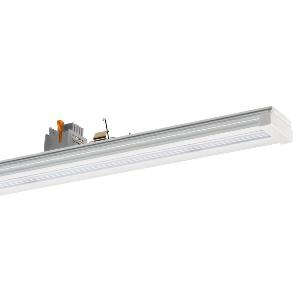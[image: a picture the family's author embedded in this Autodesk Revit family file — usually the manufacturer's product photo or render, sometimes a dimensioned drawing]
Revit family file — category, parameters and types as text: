
# Revit family: conveo_-_cvg_4500_850_xn-p_da_7_226848149-00804952_2d80
name_source: partatom
category: Lighting Fixtures
units: mm (PartAtom-declared; Revit-internal decimal feet)

## family parameters
Cut with Voids When Loaded = No
Host = Face
Light Source = No
Part Type = Normal
Room Calculation Point = No
Round Connector Dimension = Use Diameter
Shared = No

## types (1)
- CONVEO - CVG 4500/850/xN-P/DA/7 (1 x LED, 4300 lm, 5000K)
    Apparent Load = 28 VA
    Approval mark = CE
    CIE Flux Codes = 57 84 97 100 100
    Color Rendering = 80-89
    Color Temperature = 5000K
    Control Gear = Electronic ballast
    Default Elevation = 1800 mm
    Description = CVG 4500/850/xN-P/DA/7|Continuous-row system|light source: LED|work equipment: Adjustable electronic ballast, digital DALI|connected load: 220-240 V, 50-60 Hz|Power consumption: approx. 28 W|luminous flux: 4300 lm|luminous efficacy: 153 lm/W|colour temperature: Cold white, ca. 5000 K|color rendering index (CRI): >= 80|chromaticity tolerance:  3 SDCM|System of protection: IP 54|class of protection: I|technology: Continuously dimmable|luminaire body|material: Aluminium|surface: Powder coatet|colour: White|lamp cover: Acrylic (PMMA), Satine|weight (net): approx. 1.9 kg|Fastening: Available separately|minimum ambient temperature: -25 ░C|maximum ambient temperature: 55 ░C|glare control: Prism optics (linear)|Approval mark: VDE - ENEC|
    Frequency = 50 Hz
    Height = 70 mm
    Lamp = 1 x LED
    Lamp Light Flux = 4300 lm
    Lamp count = 1
    Length = 1500 mm
    Luminous efficacy = 154 lm/W
    Manufacturer = Waldmann
    ModVariant = No
    Model = 226848149-00804952
    Mounting Place = Ceiling
    Mounting Type = Pendant
    Number of Poles = 1
    OnlyDefault = Yes
    Power Factor = 1
    Product Name = CONVEO - CVG 4500/850/xN-P/DA/7
    Product group = Continuous-row system (industry)
    ProductGroupID = 301
    Protection Class = Protection class I
    Protection Degree = IP 54
    RLX_Detail_Level = 1
    RlxData = <blob elided: 100057 chars, md5=f63c358e>
    Socket = socket
    Standby Power = 0 W
    System Light Flux = 4300 lm
    System Power = 28 W
    Type Comments = Product without accessories
    Type Image = 226848019-00804937-1p7.jpg
    URL = http://relux.com
    VarID = ---
    Voltage = 230 V
    Voltage Range = 220-240 V
    Weight = 0.00 kg
    Width = 64 mm

## geometry (parser evidence)
native form markers: Blend x4, Sweep x12
no freeform markers — native parametric forms only
